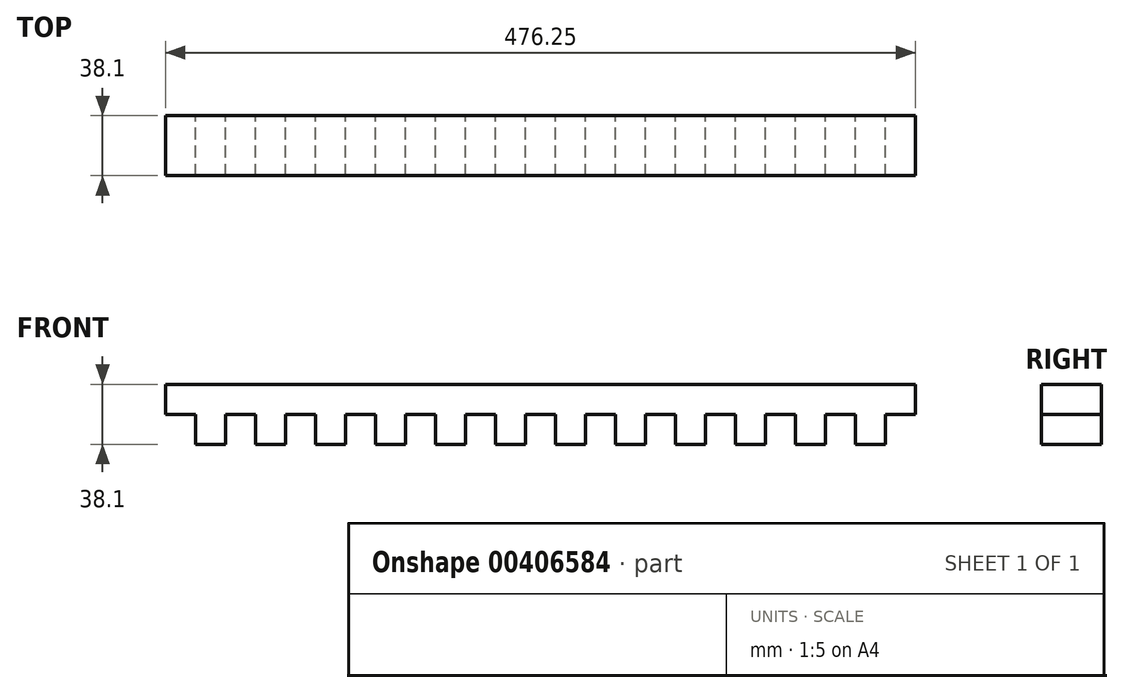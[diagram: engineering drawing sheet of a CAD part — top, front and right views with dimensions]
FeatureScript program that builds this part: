
annotation { "Feature Type Name" : "Feature", "Feature Type Description" : "" }
export const myFeature = defineFeature(function(context is Context, id is Id, definition is map)
    precondition{}
    {
        {
            var Q0;
            Q0=qCreatedBy(makeId("Front.planeOp"),FACE);
            var sketch = newSketch(context, id + "F0", { "sketchPlane" : qUnion([Q0])});
            skLineSegment(sketch, "E0", {"start": v(0, 0) * mm, "end": v(476.25, 0) * mm});
            skLineSegment(sketch, "E1", {"start": v(67.44, -38.1) * mm, "end": v(57.15, -38.1) * mm});
            skLineSegment(sketch, "E2", {"start": v(57.15, -19.05) * mm, "end": v(48.39, -19.05) * mm});
            skLineSegment(sketch, "E3", {"start": v(19.05, -38.1) * mm, "end": v(19.05, -19.05) * mm});
            skLineSegment(sketch, "E4", {"start": v(19.05, -19.05) * mm, "end": v(0, -19.05) * mm});
            skLineSegment(sketch, "E5", {"start": v(0, -19.05) * mm, "end": v(0, 0) * mm});
            skLineSegment(sketch, "E6", {"start": v(38.1, -19.05) * mm, "end": v(57.15, -19.05) * mm});
            skLineSegment(sketch, "E7", {"start": v(57.15, -19.05) * mm, "end": v(57.15, -38.1) * mm});
            skLineSegment(sketch, "E8", {"start": v(57.15, -38.1) * mm, "end": v(76.2, -38.1) * mm});
            skLineSegment(sketch, "E9", {"start": v(76.2, -38.1) * mm, "end": v(76.2, -19.05) * mm});
            skLineSegment(sketch, "E10", {"start": v(76.2, -19.05) * mm, "end": v(95.25, -19.05) * mm});
            skLineSegment(sketch, "E11", {"start": v(95.25, -19.05) * mm, "end": v(95.25, -38.1) * mm});
            skLineSegment(sketch, "E12", {"start": v(95.25, -38.1) * mm, "end": v(114.3, -38.1) * mm});
            skLineSegment(sketch, "E13", {"start": v(114.3, -38.1) * mm, "end": v(114.3, -19.05) * mm});
            skLineSegment(sketch, "E14", {"start": v(114.3, -19.05) * mm, "end": v(133.35, -19.05) * mm});
            skLineSegment(sketch, "E15", {"start": v(133.35, -19.05) * mm, "end": v(133.35, -38.1) * mm});
            skLineSegment(sketch, "E16", {"start": v(133.35, -38.1) * mm, "end": v(152.4, -38.1) * mm});
            skLineSegment(sketch, "E17", {"start": v(152.4, -38.1) * mm, "end": v(152.4, -19.05) * mm});
            skLineSegment(sketch, "E18", {"start": v(152.4, -19.05) * mm, "end": v(171.45, -19.05) * mm});
            skLineSegment(sketch, "E19", {"start": v(171.45, -19.05) * mm, "end": v(171.45, -38.1) * mm});
            skLineSegment(sketch, "E20", {"start": v(171.45, -38.1) * mm, "end": v(190.5, -38.1) * mm});
            skLineSegment(sketch, "E21", {"start": v(190.5, -38.1) * mm, "end": v(190.5, -19.05) * mm});
            skLineSegment(sketch, "E22", {"start": v(190.5, -19.05) * mm, "end": v(209.55, -19.05) * mm});
            skLineSegment(sketch, "E23", {"start": v(209.55, -19.05) * mm, "end": v(209.55, -38.1) * mm});
            skLineSegment(sketch, "E24", {"start": v(209.55, -38.1) * mm, "end": v(228.6, -38.1) * mm});
            skLineSegment(sketch, "E25", {"start": v(228.6, -38.1) * mm, "end": v(228.6, -19.05) * mm});
            skLineSegment(sketch, "E26", {"start": v(228.6, -19.05) * mm, "end": v(247.65, -19.05) * mm});
            skLineSegment(sketch, "E27", {"start": v(247.65, -19.05) * mm, "end": v(247.65, -38.1) * mm});
            skLineSegment(sketch, "E28", {"start": v(247.65, -38.1) * mm, "end": v(266.7, -38.1) * mm});
            skLineSegment(sketch, "E29", {"start": v(266.7, -38.1) * mm, "end": v(266.7, -19.05) * mm});
            skLineSegment(sketch, "E30", {"start": v(266.7, -19.05) * mm, "end": v(285.75, -19.05) * mm});
            skLineSegment(sketch, "E31", {"start": v(285.75, -19.05) * mm, "end": v(285.75, -38.1) * mm});
            skLineSegment(sketch, "E32", {"start": v(285.75, -38.1) * mm, "end": v(304.8, -38.1) * mm});
            skLineSegment(sketch, "E33", {"start": v(304.8, -38.1) * mm, "end": v(304.8, -19.05) * mm});
            skLineSegment(sketch, "E34", {"start": v(304.8, -19.05) * mm, "end": v(323.85, -19.05) * mm});
            skLineSegment(sketch, "E35", {"start": v(323.85, -19.05) * mm, "end": v(323.85, -38.1) * mm});
            skLineSegment(sketch, "E36", {"start": v(323.85, -38.1) * mm, "end": v(342.9, -38.1) * mm});
            skLineSegment(sketch, "E37", {"start": v(342.9, -38.1) * mm, "end": v(342.9, -19.05) * mm});
            skLineSegment(sketch, "E38", {"start": v(342.9, -19.05) * mm, "end": v(361.95, -19.05) * mm});
            skLineSegment(sketch, "E39", {"start": v(361.95, -19.05) * mm, "end": v(361.95, -38.1) * mm});
            skLineSegment(sketch, "E40", {"start": v(361.95, -38.1) * mm, "end": v(381, -38.1) * mm});
            skLineSegment(sketch, "E41", {"start": v(381, -38.1) * mm, "end": v(381, -19.05) * mm});
            skLineSegment(sketch, "E42", {"start": v(381, -19.05) * mm, "end": v(400.05, -19.05) * mm});
            skLineSegment(sketch, "E43", {"start": v(400.05, -19.05) * mm, "end": v(400.05, -38.1) * mm});
            skLineSegment(sketch, "E44", {"start": v(400.05, -38.1) * mm, "end": v(419.1, -38.1) * mm});
            skLineSegment(sketch, "E45", {"start": v(419.1, -38.1) * mm, "end": v(419.1, -19.05) * mm});
            skLineSegment(sketch, "E46", {"start": v(419.1, -19.05) * mm, "end": v(438.15, -19.05) * mm});
            skLineSegment(sketch, "E47", {"start": v(438.15, -19.05) * mm, "end": v(438.15, -38.1) * mm});
            skLineSegment(sketch, "E48", {"start": v(438.15, -38.1) * mm, "end": v(457.2, -38.1) * mm});
            skLineSegment(sketch, "E49", {"start": v(457.2, -38.1) * mm, "end": v(457.2, -19.05) * mm});
            skLineSegment(sketch, "E50", {"start": v(457.2, -19.05) * mm, "end": v(476.25, -19.05) * mm});
            skLineSegment(sketch, "E51", {"start": v(476.25, -19.05) * mm, "end": v(476.25, 0) * mm});
            skPoint(sketch, "E52.end.orphan", {"position": v(542.16, 0) * mm});
            skPoint(sketch, "E53.end.orphan", {"position": v(533.4, -19.05) * mm});
            skPoint(sketch, "E54.end.orphan", {"position": v(514.35, -38.1) * mm});
            skPoint(sketch, "E55.end.orphan", {"position": v(495.3, -19.05) * mm});
            skPoint(sketch, "E56.start.orphan", {"position": v(476.25, -38.1) * mm});
            skPoint(sketch, "E57.end.orphan", {"position": v(1026.29, -19.05) * mm});
            skPoint(sketch, "E58.end.orphan", {"position": v(67.44, -19.05) * mm});
            skPoint(sketch, "E59.orphan", {"position": v(48.39, -38.1) * mm});
            skLineSegment(sketch, "E60", {"start": v(19.05, -38.1) * mm, "end": v(38.1, -38.1) * mm});
            skLineSegment(sketch, "E61", {"start": v(38.1, -38.1) * mm, "end": v(38.1, -19.05) * mm});
            skSolve(sketch);
        }
        {
            var Q0;
            Q0=makeQuery(id+"F0.imprint","IMPRINT",FACE,{"disambiguationData":[TD([[makeQuery(id+"F0.imprint","IMPRINT",EDGE,{"derivedFrom":sQuery(id+"F0.wireOp",EDGE,"E0")}),-1.0]])]});
            extrude(context, id + "F1", {"entities" : qUnion([Q0]), "depth" : 38.1 * mm});
        }
    });
